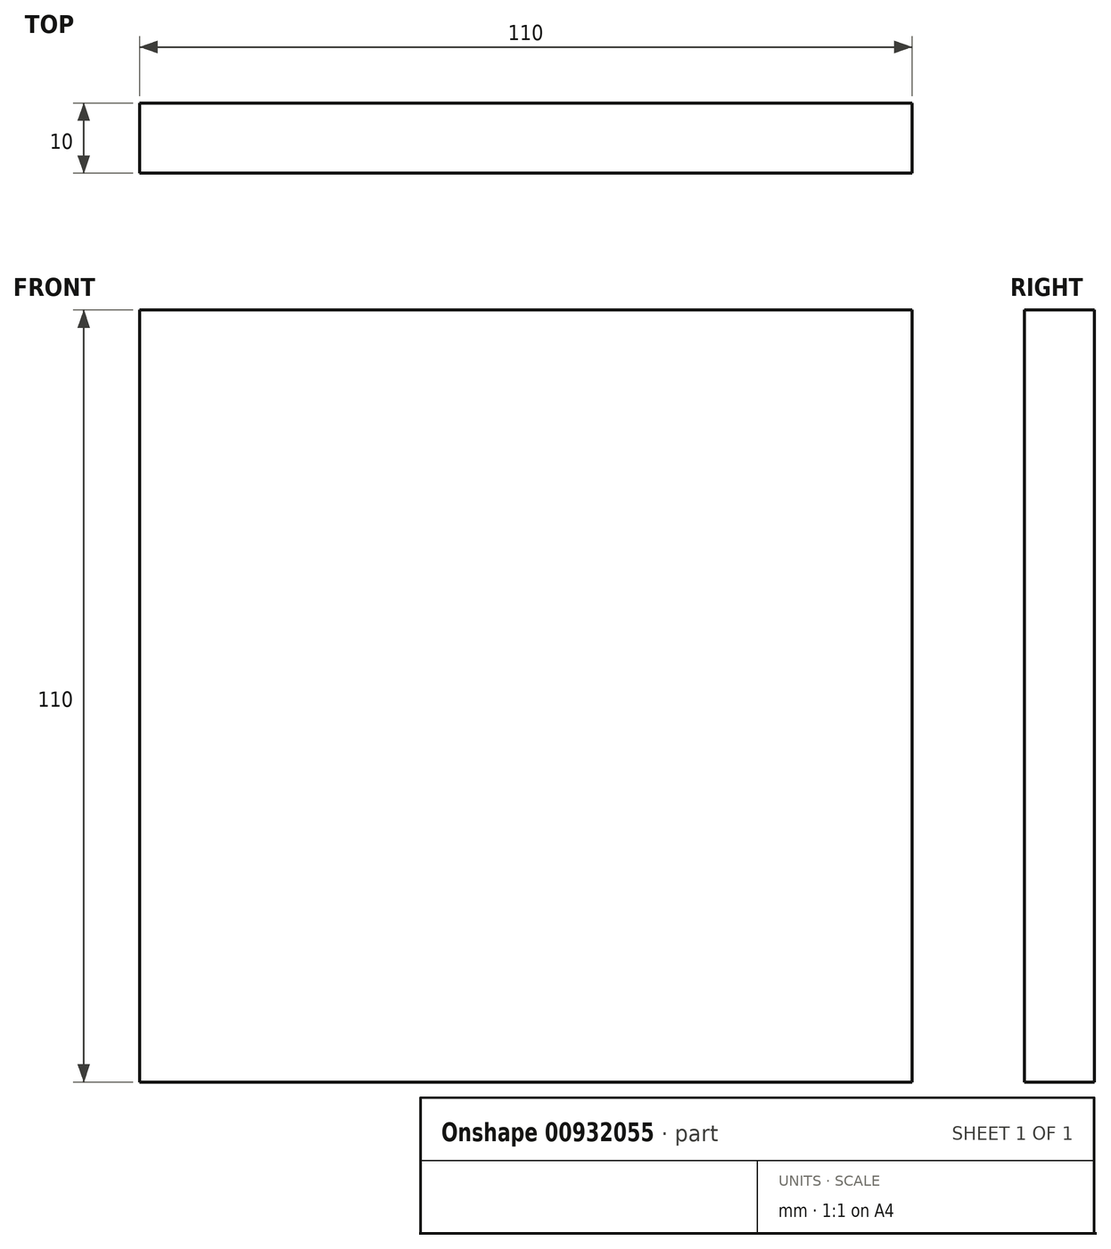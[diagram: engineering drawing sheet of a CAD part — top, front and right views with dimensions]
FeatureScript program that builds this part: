
annotation { "Feature Type Name" : "Feature", "Feature Type Description" : "" }
export const myFeature = defineFeature(function(context is Context, id is Id, definition is map)
    precondition{}
    {
        {
            var Q0;
            Q0=qCreatedBy(makeId("Front.planeOp"),FACE);
            var sketch = newSketch(context, id + "F0", { "sketchPlane" : qUnion([Q0])});
            skLineSegment(sketch, "E0.bottom", {"start": v(0, 0) * mm, "end": v(110, 0) * mm});
            skLineSegment(sketch, "E0.top", {"start": v(0, 110) * mm, "end": v(110, 110) * mm});
            skLineSegment(sketch, "E0.left", {"start": v(0, 0) * mm, "end": v(0, 110) * mm});
            skLineSegment(sketch, "E0.right", {"start": v(110, 0) * mm, "end": v(110, 110) * mm});
            skSolve(sketch);
        }
        {
            var Q0;
            Q0 = qSketchRegion(id + "F0", true);
            extrude(context, id + "F1", {"entities" : qUnion([Q0]), "depth" : 10 * mm, "offsetDistance" : 25 * mm});
        }
    });
